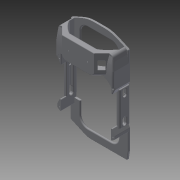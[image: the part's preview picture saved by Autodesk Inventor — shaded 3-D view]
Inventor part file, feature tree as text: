
AUTODESK INVENTOR PART (.ipt)
format: ipt  version: 2015 (Build 190159000, 159)  size: 1,506,816 bytes
history: native  units: mm
features: fillet x47, extrude x34, sketch x26, chamfer x7
ambient origin geometry x8: Origin, YZ Plane, XZ Plane, XY Plane, X Axis, Y Axis, Z Axis, Center Point
bodies: Body1 (feature_tree)
feature tree (114):
  sketch  "Sketch1"  dims[d35=5.0mm d36=0.0mm d40=5.0mm d41=0.0mm]
  extrude  "Extrusion3"  Depth=5.0mm TaperAngle=0.0deg
  extrude  "Extrusion4"  Depth=5.0mm TaperAngle=0.0deg
  fillet  "Fillet1"  Radius=56.0mm
  extrude  "Extrusion5"  Depth=5.0mm
  extrude  "Extrusion6"  Depth=5.0mm TaperAngle=0.0deg
  extrude  "Extrusion7"  Depth=5.0mm
  sketch  "Sketch3"  dims[d46=5.0mm d47=5.0mm]
  extrude  "Extrusion8"  Depth=151.0mm
  extrude  "Extrusion17"  Depth=5.0mm TaperAngle=0.0deg
  extrude  "Extrusion18"  Depth=5.0mm
  extrude  "Extrusion19"  Depth=100.0mm
  sketch  "Sketch17"  dims[d85=5.0mm d86=48.5mm d87=0.0mm]
  extrude  "Extrusion20"  Depth=10.0mm
  extrude  "Extrusion21"  Depth=10.0mm
  sketch  "Sketch18"  dims[d88=5.0mm d89=0.0mm d90=3.0mm]
  extrude  "Extrusion22"  Depth=10.0mm
  extrude  "Extrusion23"  Depth=5.0mm TaperAngle=0.0deg
  extrude  "Extrusion24"  Depth=10.0mm
  extrude  "Extrusion25"  Depth=10.0mm
  fillet  "Fillet3"  Radius=10.0mm
  extrude  "Extrusion26"  Depth=5.0mm TaperAngle=0.0deg
  sketch  "Sketch23"  dims[d97=10.0mm d99=10.0mm]
  extrude  "Extrusion27"  Depth=10.0mm
  extrude  "Extrusion28"  Depth=10.0mm
  sketch  "Sketch24"  dims[d100=10.0mm d102=10.0mm]
  sketch  "Sketch25"  dims[d104=10.0mm d105=5.0mm d106=0.0mm]
  extrude  "Extrusion33"  Depth=40.0mm TaperAngle=0.0deg
  chamfer  "Chamfer1"  Distance=45.0mm
  fillet  "Fillet4"  Radius=9.0mm
  chamfer  "Chamfer2"  Distance=4.0mm
  chamfer  "Chamfer3"  Distance=5.0mm
  chamfer  "Chamfer4"  Distance=16.0mm Angle=45.0deg
  chamfer  "Chamfer5"  Distance=10.0mm
  chamfer  "Chamfer6"  Distance=4.0mm Angle=45.0deg
  chamfer  "Chamfer7"  Distance=5.65mm Angle=45.0deg
  extrude  "Extrusion35"  Depth=1.0mm TaperAngle=45.0deg
  extrude  "Extrusion36"  Depth=1.0mm TaperAngle=45.0deg
  fillet  "Fillet5"  Radius=2.724mm
  fillet  "Fillet6"  Radius=2.663mm
  fillet  "Fillet7"  Radius=5.0mm
  fillet  "Fillet8"  Radius=37.0mm
  fillet  "Fillet9"  Radius=20.0mm
  fillet  "Fillet10"  Radius=2.0mm
  fillet  "Fillet11"  Radius=5.0mm
  fillet  "Fillet12"  Radius=2.0mm
  fillet  "Fillet14"  Radius=2.0mm
  fillet  "Fillet15"  Radius=10.0mm
  fillet  "Fillet16"  Radius=2.0mm
  fillet  "Fillet17"  Radius=2.0mm
  fillet  "Fillet18"  Radius=8.0mm
  fillet  "Fillet19"  Radius=300.0mm
  fillet  "Fillet20"  Radius=1.0mm
  fillet  "Fillet21"  Radius=4.0mm
  fillet  "Fillet22"  Radius=4.0mm
  fillet  "Fillet23"  Radius=4.0mm
  fillet  "Fillet24"  Radius=3.5mm
  fillet  "Fillet25"  Radius=1.0mm
  fillet  "Fillet26"  Radius=4.0mm
  fillet  "Fillet27"  Radius=10.0mm
  fillet  "Fillet28"  Radius=2.0mm
  extrude  "Extrusion37"  Depth=1.0mm
  fillet  "Fillet29"  Radius=2.0mm
  fillet  "Fillet30"  Radius=2.0mm
  fillet  "Fillet31"  Radius=3.0mm
  fillet  "Fillet32"  Radius=4.0mm
  fillet  "Fillet33"  Radius=2.0mm
  fillet  "Fillet34"  Radius=3.0mm
  fillet  "Fillet35"  Radius=3.0mm
  extrude  "Extrusion38"  Depth=1.0mm
  fillet  "Fillet36"  Radius=2.0mm
  extrude  "Extrusion40"  Depth=1.0mm
  fillet  "Fillet37"  Radius=2.0mm
  extrude  "Extrusion41"  Depth=1.0mm
  fillet  "Fillet38"  Radius=21.0mm
  fillet  "Fillet39"  Radius=20.75mm
  extrude  "Extrusion42"  Depth=1.0mm
  sketch  "Sketch32"  dims[d124=40.0mm d125=0.0mm d126=45.0mm d127=0.0mm]
  sketch  "Sketch33"  dims[d129=80.0mm]
  sketch  "Sketch34"  dims[d132=116.0mm]
  sketch  "Sketch35"  dims[d133=32.0mm d134=45.0mm d135=0.0mm d142=9.0mm]
  extrude  "Extrusion43"  Depth=1.0mm
  extrude  "Extrusion44"  Depth=1.0mm
  extrude  "Extrusion45"  Depth=1.0mm TaperAngle=0.0deg
  extrude  "Extrusion46"  Depth=1.0mm
  extrude  "Extrusion47"  Depth=1.0mm TaperAngle=0.0deg
  fillet  "Fillet41"  Radius=1.3mm
  extrude  "Extrusion48"  Depth=1.0mm
  fillet  "Fillet42"  Radius=3.0mm
  fillet  "Fillet43"  Radius=3.0mm
  fillet  "Fillet44"  Radius=3.0mm
  fillet  "Fillet45"  Radius=3.0mm
  fillet  "Fillet46"  Radius=40.0mm
  extrude  "Extrusion49"  Depth=1.0mm TaperAngle=0.0deg
  extrude  "Extrusion50"  Depth=1.0mm TaperAngle=0.0deg
  fillet  "Fillet47"  Radius=20.0mm
  fillet  "Fillet48"  Radius=20.0mm
  fillet  "Fillet49"  Radius=8.0mm
  fillet  "Fillet50"  Radius=100.0mm
  sketch  "Sketch2"  dims[d42=20.0mm d43=5.0mm d44=0.0mm d45=56.0mm]
  sketch  "Sketch14"  dims[d48=5.0mm d49=45.0mm d50=0.0mm]
  sketch  "Sketch15"  dims[d51=5.0mm d52=0.0mm d54=35.0mm]
  sketch  "Sketch16"  dims[d55=35.0mm d56=0.0mm d84=151.0mm]
  sketch  "Sketch20"  dims[d91=3.0mm d92=100.0mm]
  sketch  "Sketch22"  dims[d93=5.0mm d94=0.0mm d95=10.0mm]
  sketch  "Sketch26"  dims[d107=5.0mm d108=0.0mm d109=10.0mm]
  sketch  "Sketch28"  dims[d111=10.0mm d113=10.0mm d114=10.0mm]
  sketch  "Sketch29"  dims[d116=10.0mm d117=5.0mm d118=0.0mm]
  sketch  "Sketch30"  dims[d119=5.0mm d120=0.0mm d121=10.0mm]
  sketch  "Sketch31"  dims[d122=10.0mm d123=10.0mm]
  sketch  "Sketch36"  dims[d143=45.0mm]
  sketch  "Sketch37"  dims[d144=45.0mm d145=4.0mm d146=0.0mm]
  sketch  "Sketch38"  dims[d147=4.0mm d148=5.0mm d149=0.0mm d150=0.0mm]
  sketch  "Sketch39"  dims[d163=90.0mm d174=5.0mm d175=0.0mm d178=16.0mm d179=2.0mm d180=45.0deg d181=10.0mm d182=4.0mm d183=2.0mm d184=45.0deg d185=5.65mm d186=2.0mm d187=45.0deg d188=10.43mm d189=2.0mm d190=45.0deg d191=10.43mm d192=2.0mm d193=45.0deg d194=2.724mm d195=2.0mm d196=45.0deg d197=2.663mm d198=2.0mm d199=45.0deg d200=5.0mm d201=0.0mm d202=37.0mm d203=0.0mm d204=20.0mm d205=2.0mm d206=5.0mm d207=2.0mm d208=2.0mm d209=10.0mm d210=2.0mm d211=2.0mm d213=8.0mm d214=300.0mm d215=1.0mm d216=4.0mm d217=4.0mm d218=4.0mm d219=3.5mm d220=1.0mm d221=4.0mm d222=10.0mm d223=2.0mm d224=2.0mm d225=2.0mm d226=2.0mm d227=3.0mm d228=4.0mm d229=0.0mm d230=2.0mm d231=3.0mm d232=3.0mm d233=4.0mm d234=2.0mm d235=3.0mm d236=2.0mm d237=15.0mm d238=21.0mm d239=20.75mm d240=0.0mm d241=1.0mm d242=122.0mm d245=135.3mm d246=20.75mm d247=0.0mm d248=1.0mm d249=20.0mm d250=0.0mm d251=1.3mm d252=0.2mm d257=3.0mm d258=3.0mm d262=3.0mm d263=3.0mm d264=40.0mm d265=0.0mm d266=20.0mm d267=0.0mm d268=20.0mm d269=0.0mm d270=20.0mm d271=0.0mm d272=20.0mm d273=0.0mm d274=8.0mm d275=100.0mm d276=35.0mm d277=0.0mm d279=2.0mm d280=8.0mm d281=100.0mm d282=35.0mm d283=0.0mm d284=2.0mm d285=2.0mm d286=2.0mm d287=2.0mm d288=2.0mm d290=16.0mm d291=16.0mm d292=3.0mm d293=3.0mm d294=15.0mm d295=0.0mm d297=5.0mm d298=0.0mm d299=2.0mm d300=40.0mm d301=1.0mm d302=1.0mm]
